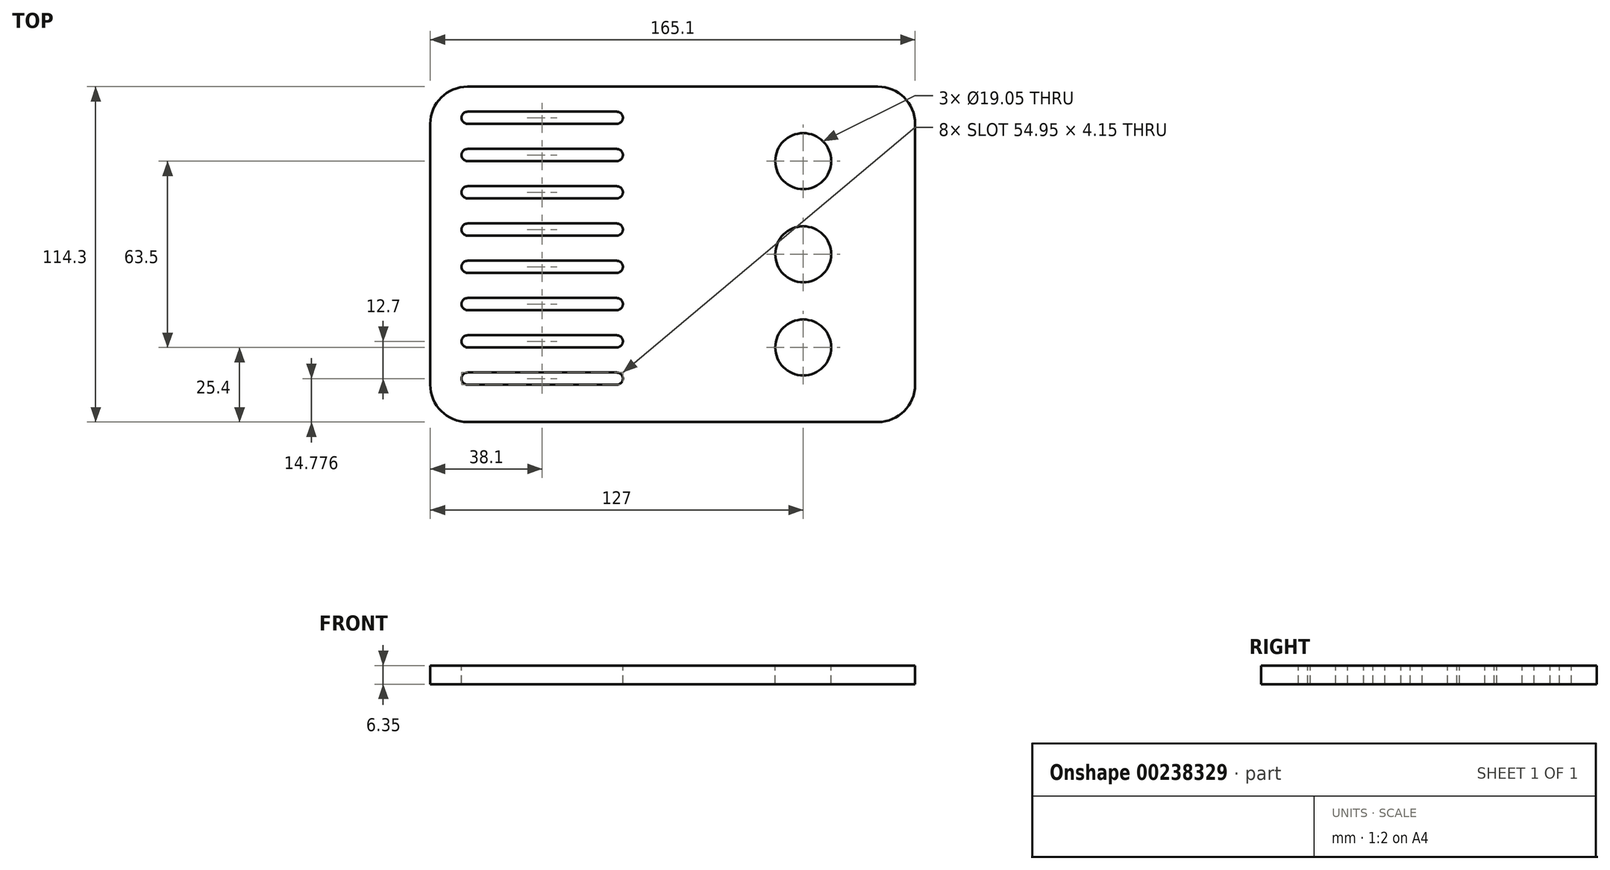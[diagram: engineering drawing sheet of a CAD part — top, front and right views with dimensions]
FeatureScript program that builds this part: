
annotation { "Feature Type Name" : "Feature", "Feature Type Description" : "" }
export const myFeature = defineFeature(function(context is Context, id is Id, definition is map)
    precondition{}
    {
        {
            var Q0;
            Q0=qCreatedBy(makeId("Top.planeOp"),FACE);
            var sketch = newSketch(context, id + "F0", { "sketchPlane" : qUnion([Q0])});
            skLineSegment(sketch, "E0.bottom", {"start": v(69.85, 57.15) * mm, "end": v(-69.85, 57.15) * mm});
            skLineSegment(sketch, "E0.top", {"start": v(69.85, -57.15) * mm, "end": v(-69.85, -57.15) * mm});
            skLineSegment(sketch, "E0.left", {"start": v(82.55, 44.45) * mm, "end": v(82.55, -44.45) * mm});
            skLineSegment(sketch, "E0.right", {"start": v(-82.55, 44.45) * mm, "end": v(-82.55, -44.45) * mm});
            skPoint(sketch, "E0.middle", {"position": v(0, 0) * mm});
            skPoint(sketch, "E1.visualSharp", {"position": v(-82.55, 57.15) * mm});
            skArc(sketch, "E1.filletArc", {"start": v(-69.85, 57.15) * mm, "mid": v(-78.83, 53.43) * mm, "end": v(-82.55, 44.45) * mm});
            skPoint(sketch, "E2.visualSharp", {"position": v(82.55, 57.15) * mm});
            skArc(sketch, "E2.filletArc", {"start": v(82.55, 44.45) * mm, "mid": v(78.83, 53.43) * mm, "end": v(69.85, 57.15) * mm});
            skPoint(sketch, "E3.visualSharp", {"position": v(82.55, -57.15) * mm});
            skArc(sketch, "E3.filletArc", {"start": v(69.85, -57.15) * mm, "mid": v(78.83, -53.43) * mm, "end": v(82.55, -44.45) * mm});
            skPoint(sketch, "E4.visualSharp", {"position": v(-82.55, -57.15) * mm});
            skArc(sketch, "E4.filletArc", {"start": v(-82.55, -44.45) * mm, "mid": v(-78.83, -53.43) * mm, "end": v(-69.85, -57.15) * mm});
            skSolve(sketch);
        }
        {
            var Q0;
            Q0=makeQuery(id+"F0.imprint","IMPRINT",FACE,{"disambiguationData":[TD([[makeQuery(id+"F0.imprint","IMPRINT",EDGE,{"derivedFrom":sQuery(id+"F0.wireOp",EDGE,"E0.bottom")}),1.0]])]});
            extrude(context, id + "F1", {"entities" : qUnion([Q0]), "depth" : 6.35 * mm});
        }
        {
            var Q0;
            Q0=makeQuery(id+"F1.opExtrude","CAP_FACE",FACE,{"disambiguationData":[OSD([sQuery(id+"F0.wireOp",EDGE,"E0.bottom"),sQuery(id+"F0.wireOp",EDGE,"E0.top"),sQuery(id+"F0.wireOp",EDGE,"E0.left"),sQuery(id+"F0.wireOp",EDGE,"E0.right"),sQuery(id+"F0.wireOp",EDGE,"E1.filletArc"),sQuery(id+"F0.wireOp",EDGE,"E2.filletArc"),sQuery(id+"F0.wireOp",EDGE,"E3.filletArc"),sQuery(id+"F0.wireOp",EDGE,"E4.filletArc")])],"isStart":false});
            var sketch = newSketch(context, id + "F2", { "sketchPlane" : qUnion([Q0])});
            skLineSegment(sketch, "E5.bottom", {"start": v(-69.85, -44.45) * mm, "end": v(-19.05, -44.45) * mm});
            skLineSegment(sketch, "E5.top", {"start": v(-69.85, -40.3) * mm, "end": v(-19.05, -40.3) * mm});
            skArc(sketch, "E6", {"start": v(-69.85, -40.3) * mm, "mid": v(-71.93, -42.37) * mm, "end": v(-69.85, -44.45) * mm});
            skArc(sketch, "E7", {"start": v(-19.05, -44.45) * mm, "mid": v(-16.97, -42.37) * mm, "end": v(-19.05, -40.3) * mm});
            skLineSegment(sketch, "E8", {"start": v(0, -51.4) * mm, "end": v(0, 12.74) * mm});
            skLineSegment(sketch, "E9.0.1.0", {"start": v(-69.85, -27.6) * mm, "end": v(-19.05, -27.6) * mm});
            skLineSegment(sketch, "E9.0.1.1", {"start": v(-69.85, -31.75) * mm, "end": v(-19.05, -31.75) * mm});
            skArc(sketch, "E9.0.1.2", {"start": v(-19.05, -31.75) * mm, "mid": v(-16.97, -29.67) * mm, "end": v(-19.05, -27.6) * mm});
            skArc(sketch, "E9.0.1.3", {"start": v(-69.85, -27.6) * mm, "mid": v(-71.93, -29.67) * mm, "end": v(-69.85, -31.75) * mm});
            skLineSegment(sketch, "E9.0.2.0", {"start": v(-69.85, -14.9) * mm, "end": v(-19.05, -14.9) * mm});
            skLineSegment(sketch, "E9.0.2.1", {"start": v(-69.85, -19.05) * mm, "end": v(-19.05, -19.05) * mm});
            skArc(sketch, "E9.0.2.2", {"start": v(-19.05, -19.05) * mm, "mid": v(-16.97, -16.97) * mm, "end": v(-19.05, -14.9) * mm});
            skArc(sketch, "E9.0.2.3", {"start": v(-69.85, -14.9) * mm, "mid": v(-71.93, -16.97) * mm, "end": v(-69.85, -19.05) * mm});
            skLineSegment(sketch, "E9.0.3.0", {"start": v(-69.85, -2.2) * mm, "end": v(-19.05, -2.2) * mm});
            skLineSegment(sketch, "E9.0.3.1", {"start": v(-69.85, -6.35) * mm, "end": v(-19.05, -6.35) * mm});
            skArc(sketch, "E9.0.3.2", {"start": v(-19.05, -6.35) * mm, "mid": v(-16.97, -4.27) * mm, "end": v(-19.05, -2.2) * mm});
            skArc(sketch, "E9.0.3.3", {"start": v(-69.85, -2.2) * mm, "mid": v(-71.93, -4.27) * mm, "end": v(-69.85, -6.35) * mm});
            skLineSegment(sketch, "E9.0.4.0", {"start": v(-69.85, 10.5) * mm, "end": v(-19.05, 10.5) * mm});
            skLineSegment(sketch, "E9.0.4.1", {"start": v(-69.85, 6.35) * mm, "end": v(-19.05, 6.35) * mm});
            skArc(sketch, "E9.0.4.2", {"start": v(-19.05, 6.35) * mm, "mid": v(-16.97, 8.43) * mm, "end": v(-19.05, 10.5) * mm});
            skArc(sketch, "E9.0.4.3", {"start": v(-69.85, 10.5) * mm, "mid": v(-71.93, 8.43) * mm, "end": v(-69.85, 6.35) * mm});
            skLineSegment(sketch, "E9.0.5.0", {"start": v(-69.85, 23.2) * mm, "end": v(-19.05, 23.2) * mm});
            skLineSegment(sketch, "E9.0.5.1", {"start": v(-69.85, 19.05) * mm, "end": v(-19.05, 19.05) * mm});
            skArc(sketch, "E9.0.5.2", {"start": v(-19.05, 19.05) * mm, "mid": v(-16.97, 21.13) * mm, "end": v(-19.05, 23.2) * mm});
            skArc(sketch, "E9.0.5.3", {"start": v(-69.85, 23.2) * mm, "mid": v(-71.93, 21.13) * mm, "end": v(-69.85, 19.05) * mm});
            skLineSegment(sketch, "E9.0.6.0", {"start": v(-69.85, 35.9) * mm, "end": v(-19.05, 35.9) * mm});
            skLineSegment(sketch, "E9.0.6.1", {"start": v(-69.85, 31.75) * mm, "end": v(-19.05, 31.75) * mm});
            skArc(sketch, "E9.0.6.2", {"start": v(-19.05, 31.75) * mm, "mid": v(-16.97, 33.83) * mm, "end": v(-19.05, 35.9) * mm});
            skArc(sketch, "E9.0.6.3", {"start": v(-69.85, 35.9) * mm, "mid": v(-71.93, 33.83) * mm, "end": v(-69.85, 31.75) * mm});
            skLineSegment(sketch, "E9.0.7.0", {"start": v(-69.85, 48.6) * mm, "end": v(-19.05, 48.6) * mm});
            skLineSegment(sketch, "E9.0.7.1", {"start": v(-69.85, 44.45) * mm, "end": v(-19.05, 44.45) * mm});
            skArc(sketch, "E9.0.7.2", {"start": v(-19.05, 44.45) * mm, "mid": v(-16.97, 46.53) * mm, "end": v(-19.05, 48.6) * mm});
            skArc(sketch, "E9.0.7.3", {"start": v(-69.85, 48.6) * mm, "mid": v(-71.93, 46.53) * mm, "end": v(-69.85, 44.45) * mm});
            skLineSegment(sketch, "E9.direction1", {"start": v(-69.85, -40.3) * mm, "end": v(-44.45, -40.3) * mm, "construction": true});
            skLineSegment(sketch, "E9.direction2", {"start": v(-69.85, -40.3) * mm, "end": v(-69.85, -27.6) * mm, "construction": true});
            skSolve(sketch);
        }
        {
            var Q0;
            Q0 = qSketchRegion(id + "F2", true);
            extrude(context, id + "F3", {"entities" : qUnion([Q0]), "operationType" : NewBodyOperationType.REMOVE, "endBound" : BoundingType.THROUGH_ALL, "oppositeDirection" : true, "depth" : 25.4 * mm});
        }
        {
            var Q0;
            Q0=makeQuery(id+"F1.opExtrude","CAP_FACE",FACE,{"disambiguationData":[OSD([sQuery(id+"F0.wireOp",EDGE,"E0.bottom"),sQuery(id+"F0.wireOp",EDGE,"E0.top"),sQuery(id+"F0.wireOp",EDGE,"E0.left"),sQuery(id+"F0.wireOp",EDGE,"E0.right"),sQuery(id+"F0.wireOp",EDGE,"E1.filletArc"),sQuery(id+"F0.wireOp",EDGE,"E2.filletArc"),sQuery(id+"F0.wireOp",EDGE,"E3.filletArc"),sQuery(id+"F0.wireOp",EDGE,"E4.filletArc")])],"isStart":false});
            var sketch = newSketch(context, id + "F4", { "sketchPlane" : qUnion([Q0])});
            skCircle(sketch, "E10", {"center": v(44.45, -31.75) * mm, "radius": 9.53 * mm});
            skCircle(sketch, "E11.0.1.0", {"center": v(44.45, 0) * mm, "radius": 9.53 * mm});
            skCircle(sketch, "E11.0.2.0", {"center": v(44.45, 31.75) * mm, "radius": 9.53 * mm});
            skLineSegment(sketch, "E11.direction1", {"start": v(44.45, -31.75) * mm, "end": v(69.85, -31.75) * mm, "construction": true});
            skLineSegment(sketch, "E11.direction2", {"start": v(44.45, -31.75) * mm, "end": v(44.45, 0) * mm, "construction": true});
            skSolve(sketch);
        }
        {
            var Q0;
            Q0=makeQuery(id+"F4.imprint","IMPRINT",FACE,{"disambiguationData":[TD([[makeQuery(id+"F4.imprint","IMPRINT",EDGE,{"derivedFrom":sQuery(id+"F4.wireOp",EDGE,"E11.0.1.0")}),1.0]])]});
            var Q1;
            Q1=makeQuery(id+"F4.imprint","IMPRINT",FACE,{"disambiguationData":[TD([[makeQuery(id+"F4.imprint","IMPRINT",EDGE,{"derivedFrom":sQuery(id+"F4.wireOp",EDGE,"E10")}),1.0]])]});
            var Q2;
            Q2=makeQuery(id+"F4.imprint","IMPRINT",FACE,{"disambiguationData":[TD([[makeQuery(id+"F4.imprint","IMPRINT",EDGE,{"derivedFrom":sQuery(id+"F4.wireOp",EDGE,"E11.0.2.0")}),1.0]])]});
            extrude(context, id + "F5", {"entities" : qUnion([Q0, Q1, Q2]), "operationType" : NewBodyOperationType.REMOVE, "endBound" : BoundingType.THROUGH_ALL, "oppositeDirection" : true, "depth" : 25.4 * mm});
        }
    });
